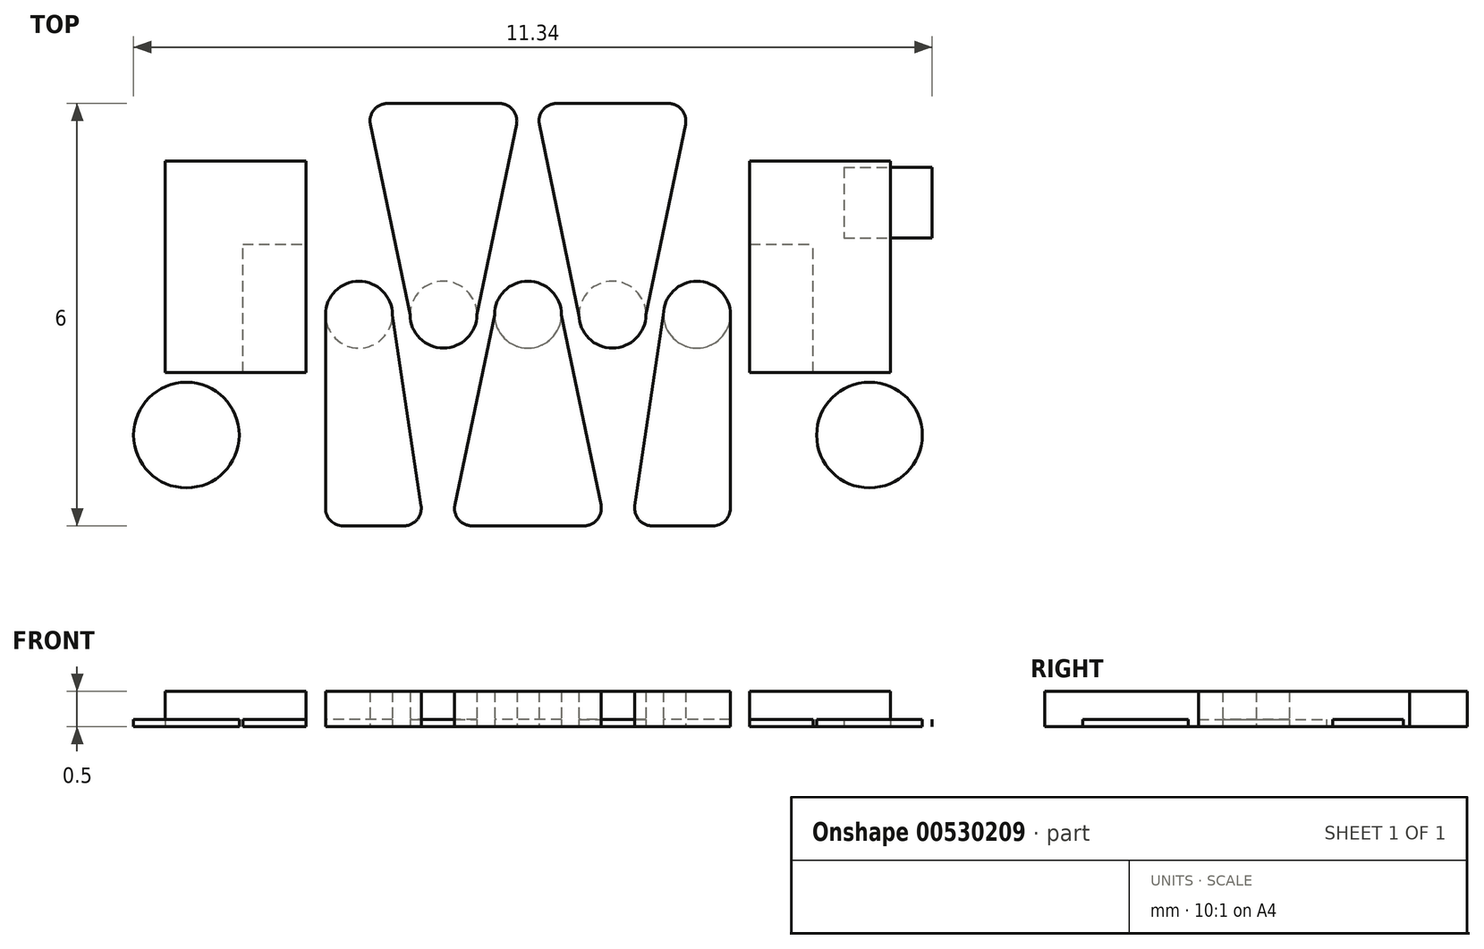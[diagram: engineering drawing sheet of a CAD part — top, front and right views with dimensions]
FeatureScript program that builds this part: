
annotation { "Feature Type Name" : "Feature", "Feature Type Description" : "" }
export const myFeature = defineFeature(function(context is Context, id is Id, definition is map)
    precondition{}
    {
        {
            var Q0;
            Q0=qCreatedBy(makeId("Top.planeOp"),FACE);
            var sketch = newSketch(context, id + "F0", { "sketchPlane" : qUnion([Q0])});
            skCircle(sketch, "E0", {"center": v(0, 0) * mm, "radius": 0.48 * mm});
            skCircle(sketch, "E1", {"center": v(1.2, 0) * mm, "radius": 0.47 * mm});
            skCircle(sketch, "E2", {"center": v(2.4, 0) * mm, "radius": 0.47 * mm});
            skCircle(sketch, "E3", {"center": v(-1.2, 0) * mm, "radius": 0.47 * mm});
            skCircle(sketch, "E4", {"center": v(-2.4, 0) * mm, "radius": 0.47 * mm});
            skLineSegment(sketch, "E5", {"start": v(0, 0) * mm, "end": v(3.15, 0) * mm, "construction": true});
            skLineSegment(sketch, "E6.bottom", {"start": v(3.15, -0.82) * mm, "end": v(4.05, -0.82) * mm});
            skLineSegment(sketch, "E6.top", {"start": v(3.15, 1) * mm, "end": v(4.05, 1) * mm});
            skLineSegment(sketch, "E6.left", {"start": v(3.15, -0.82) * mm, "end": v(3.15, 1) * mm});
            skLineSegment(sketch, "E6.right", {"start": v(4.05, -0.82) * mm, "end": v(4.05, 1) * mm});
            skLineSegment(sketch, "E7", {"start": v(3.6, 1) * mm, "end": v(3.6, -0.82) * mm, "construction": true});
            skLineSegment(sketch, "E8.bottom", {"start": v(-4.05, -0.82) * mm, "end": v(-3.15, -0.82) * mm});
            skLineSegment(sketch, "E8.top", {"start": v(-4.05, 1) * mm, "end": v(-3.15, 1) * mm});
            skLineSegment(sketch, "E8.left", {"start": v(-4.05, -0.82) * mm, "end": v(-4.05, 1) * mm});
            skLineSegment(sketch, "E8.right", {"start": v(-3.15, -0.82) * mm, "end": v(-3.15, 1) * mm});
            skLineSegment(sketch, "E9", {"start": v(-3.6, 1) * mm, "end": v(-3.6, -0.82) * mm, "construction": true});
            skLineSegment(sketch, "E10", {"start": v(0, 0) * mm, "end": v(-3.6, 0) * mm, "construction": true});
            skCircle(sketch, "E11", {"center": v(-4.85, -1.71) * mm, "radius": 0.75 * mm});
            skLineSegment(sketch, "E12", {"start": v(4.05, 0.1) * mm, "end": v(3.15, 0.09) * mm, "construction": true});
            skLineSegment(sketch, "E13", {"start": v(-3.15, 0.09) * mm, "end": v(-4.05, 0.09) * mm, "construction": true});
            skCircle(sketch, "E14.MirrorC", {"center": v(4.85, -1.71) * mm, "radius": 0.75 * mm});
            skLineSegment(sketch, "E15.bottom", {"start": v(4.49, 2.09) * mm, "end": v(5.74, 2.09) * mm});
            skLineSegment(sketch, "E15.top", {"start": v(4.49, 1.09) * mm, "end": v(5.74, 1.09) * mm});
            skLineSegment(sketch, "E15.left", {"start": v(4.49, 2.09) * mm, "end": v(4.49, 1.09) * mm});
            skLineSegment(sketch, "E15.right", {"start": v(5.74, 2.09) * mm, "end": v(5.74, 1.09) * mm});
            skSolve(sketch);
        }
        {
            var Q0;
            Q0 = qSketchRegion(id + "F0", true);
            extrude(context, id + "F1", {"entities" : qUnion([Q0]), "depth" : .1 * mm, "offsetDistance" : 25 * mm});
        }
        {
            var Q0;
            Q0=qCreatedBy(makeId("Top.planeOp"),FACE);
            var sketch = newSketch(context, id + "F2", { "sketchPlane" : qUnion([Q0])});
            skArc(sketch, "E16", {"start": v(-1.92, 0) * mm, "mid": v(-2.4, 0.47) * mm, "end": v(-2.87, 0) * mm});
            skLineSegment(sketch, "E17", {"start": v(-2.87, 0) * mm, "end": v(-2.87, -3) * mm});
            skLineSegment(sketch, "E18", {"start": v(-2.87, -3) * mm, "end": v(-1.47, -3) * mm});
            skLineSegment(sketch, "E19", {"start": v(-1.47, -3) * mm, "end": v(-1.92, 0) * mm});
            skArc(sketch, "E20", {"start": v(-1.67, 0) * mm, "mid": v(-1.2, -0.47) * mm, "end": v(-0.72, 0) * mm});
            skLineSegment(sketch, "E21", {"start": v(-1.67, 0) * mm, "end": v(-2.3, 3) * mm});
            skLineSegment(sketch, "E22", {"start": v(-2.3, 3) * mm, "end": v(-0.1, 3) * mm});
            skLineSegment(sketch, "E23", {"start": v(-0.1, 3) * mm, "end": v(-0.73, 0) * mm});
            skLineSegment(sketch, "E24", {"start": v(-1.2, 0) * mm, "end": v(-1.2, 3) * mm, "construction": true});
            skArc(sketch, "E25", {"start": v(0.48, 0) * mm, "mid": v(0, 0.48) * mm, "end": v(-0.48, 0) * mm});
            skLineSegment(sketch, "E26", {"start": v(-0.48, 0) * mm, "end": v(-1.1, -3) * mm});
            skLineSegment(sketch, "E27", {"start": v(-1.1, -3) * mm, "end": v(1.1, -3) * mm});
            skLineSegment(sketch, "E28", {"start": v(1.1, -3) * mm, "end": v(0.48, 0) * mm});
            skLineSegment(sketch, "E29", {"start": v(0, 0) * mm, "end": v(0, -3) * mm, "construction": true});
            skLineSegment(sketch, "E30.MirrorCS", {"start": v(1.67, 0) * mm, "end": v(2.3, 3) * mm});
            skLineSegment(sketch, "E31.MirrorCS", {"start": v(2.3, 3) * mm, "end": v(0.1, 3) * mm});
            skLineSegment(sketch, "E32.MirrorCS", {"start": v(0.1, 3) * mm, "end": v(0.73, 0) * mm});
            skArc(sketch, "E33.MirrorCS", {"start": v(1.67, 0) * mm, "mid": v(1.2, -0.47) * mm, "end": v(0.72, 0) * mm});
            skArc(sketch, "E34.MirrorCS", {"start": v(1.92, 0) * mm, "mid": v(2.4, 0.47) * mm, "end": v(2.87, 0) * mm});
            skLineSegment(sketch, "E35.MirrorCS", {"start": v(1.47, -3) * mm, "end": v(1.92, 0) * mm});
            skLineSegment(sketch, "E36.MirrorCS", {"start": v(2.87, -3) * mm, "end": v(1.47, -3) * mm});
            skLineSegment(sketch, "E37.MirrorCS", {"start": v(2.87, 0) * mm, "end": v(2.87, -3) * mm});
            skSolve(sketch);
        }
        {
            var Q0;
            Q0 = qSketchRegion(id + "F2", true);
            extrude(context, id + "F3", {"entities" : qUnion([Q0]), "depth" : .5 * mm, "offsetDistance" : 25 * mm});
        }
        {
            var Q0;
            Q0=qCreatedBy(makeId("Top.planeOp"),FACE);
            var sketch = newSketch(context, id + "F4", { "sketchPlane" : qUnion([Q0])});
            skLineSegment(sketch, "E38.bottom", {"start": v(-3.15, -0.82) * mm, "end": v(-5.15, -0.82) * mm});
            skLineSegment(sketch, "E38.top", {"start": v(-3.15, 2.18) * mm, "end": v(-5.15, 2.18) * mm});
            skLineSegment(sketch, "E38.left", {"start": v(-3.15, -0.82) * mm, "end": v(-3.15, 2.18) * mm});
            skLineSegment(sketch, "E38.right", {"start": v(-5.15, -0.82) * mm, "end": v(-5.15, 2.18) * mm});
            skLineSegment(sketch, "E39.MirrorCS", {"start": v(3.15, -0.82) * mm, "end": v(5.15, -0.82) * mm});
            skLineSegment(sketch, "E40.MirrorCS", {"start": v(3.15, 2.18) * mm, "end": v(5.15, 2.18) * mm});
            skLineSegment(sketch, "E41.MirrorCS", {"start": v(3.15, -0.82) * mm, "end": v(3.15, 2.18) * mm});
            skLineSegment(sketch, "E42.MirrorCS", {"start": v(5.15, -0.82) * mm, "end": v(5.15, 2.18) * mm});
            skSolve(sketch);
        }
        {
            var Q0;
            Q0 = qSketchRegion(id + "F4", true);
            extrude(context, id + "F5", {"entities" : qUnion([Q0]), "depth" : .5 * mm, "offsetDistance" : 25 * mm});
        }
        {
            var Q0;
            Q0=makeQuery(id+"F3.opExtrude","SWEPT_EDGE",EDGE,{"disambiguationData":[OSD([sQuery(id+"F2.wireOp",EDGE,"E31.MirrorCS"),sQuery(id+"F2.wireOp",EDGE,"E32.MirrorCS")])]});
            var Q1;
            Q1=makeQuery(id+"F3.opExtrude","SWEPT_EDGE",EDGE,{"disambiguationData":[OSD([sQuery(id+"F2.wireOp",EDGE,"E30.MirrorCS"),sQuery(id+"F2.wireOp",EDGE,"E31.MirrorCS")])]});
            var Q2;
            Q2=makeQuery(id+"F3.opExtrude","SWEPT_EDGE",EDGE,{"disambiguationData":[OSD([sQuery(id+"F2.wireOp",EDGE,"E22"),sQuery(id+"F2.wireOp",EDGE,"E23")])]});
            var Q3;
            Q3=makeQuery(id+"F3.opExtrude","SWEPT_EDGE",EDGE,{"disambiguationData":[OSD([sQuery(id+"F2.wireOp",EDGE,"E21"),sQuery(id+"F2.wireOp",EDGE,"E22")])]});
            var Q4;
            Q4=makeQuery(id+"F3.opExtrude","SWEPT_EDGE",EDGE,{"disambiguationData":[OSD([sQuery(id+"F2.wireOp",EDGE,"E36.MirrorCS"),sQuery(id+"F2.wireOp",EDGE,"E37.MirrorCS")])]});
            var Q5;
            Q5=makeQuery(id+"F3.opExtrude","SWEPT_EDGE",EDGE,{"disambiguationData":[OSD([sQuery(id+"F2.wireOp",EDGE,"E35.MirrorCS"),sQuery(id+"F2.wireOp",EDGE,"E36.MirrorCS")])]});
            var Q6;
            Q6=makeQuery(id+"F3.opExtrude","SWEPT_EDGE",EDGE,{"disambiguationData":[OSD([sQuery(id+"F2.wireOp",EDGE,"E27"),sQuery(id+"F2.wireOp",EDGE,"E28")])]});
            var Q7;
            Q7=makeQuery(id+"F3.opExtrude","SWEPT_EDGE",EDGE,{"disambiguationData":[OSD([sQuery(id+"F2.wireOp",EDGE,"E26"),sQuery(id+"F2.wireOp",EDGE,"E27")])]});
            var Q8;
            Q8=makeQuery(id+"F3.opExtrude","SWEPT_EDGE",EDGE,{"disambiguationData":[OSD([sQuery(id+"F2.wireOp",EDGE,"E18"),sQuery(id+"F2.wireOp",EDGE,"E19")])]});
            var Q9;
            Q9=makeQuery(id+"F3.opExtrude","SWEPT_EDGE",EDGE,{"disambiguationData":[OSD([sQuery(id+"F2.wireOp",EDGE,"E17"),sQuery(id+"F2.wireOp",EDGE,"E18")])]});
            fillet(context, id + "F6", {"entities" : qUnion([Q0, Q1, Q2, Q3, Q4, Q5, Q6, Q7, Q8, Q9]), "radius" : .25 * mm, "tangentPropagation" : true, "allowEdgeOverflow" : false});
        }
    });
